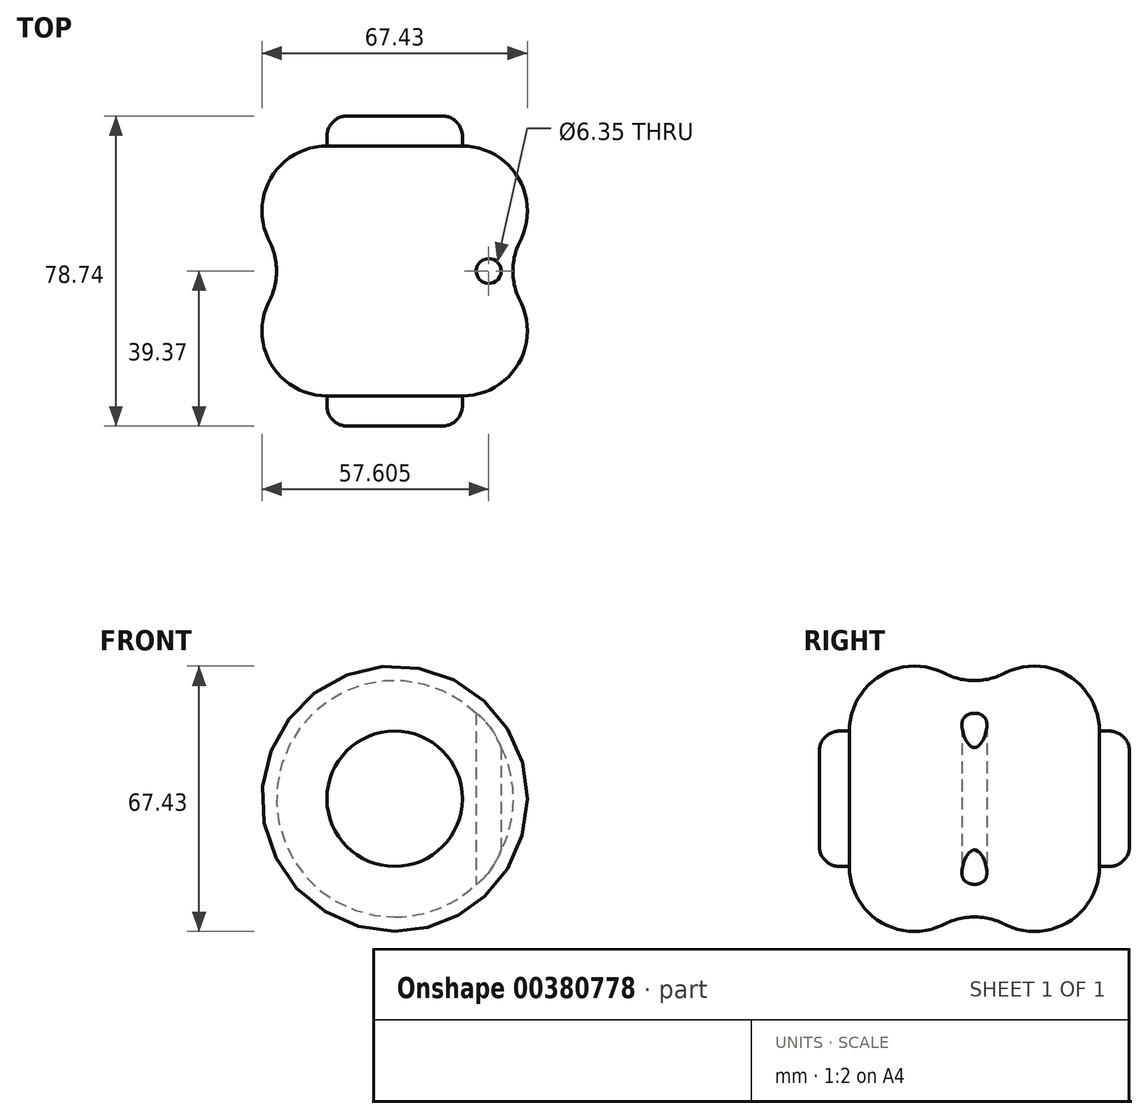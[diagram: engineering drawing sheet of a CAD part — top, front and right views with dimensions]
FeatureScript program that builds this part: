
annotation { "Feature Type Name" : "Feature", "Feature Type Description" : "" }
export const myFeature = defineFeature(function(context is Context, id is Id, definition is map)
    precondition{}
    {
        {
            var Q0;
            Q0=qCreatedBy(makeId("Front.planeOp"),FACE);
            var sketch = newSketch(context, id + "F0", { "sketchPlane" : qUnion([Q0])});
            skCircle(sketch, "E0", {"center": v(-32.36, 37.18) * mm, "radius": 28.31 * mm});
            skSolve(sketch);
        }
        {
            var Q0;
            Q0=makeQuery(id+"F0.imprint","IMPRINT",FACE,{"disambiguationData":[TD([[makeQuery(id+"F0.imprint","IMPRINT",EDGE,{"derivedFrom":sQuery(id+"F0.wireOp",EDGE,"E0")}),1.0]])]});
            extrude(context, id + "F1", {"entities" : qUnion([Q0]), "depth" : 31.75 * mm, "hasDraft" : true, "draftAngle" : 25 * degree, "hasSecondDirection" : true, "secondDirectionOppositeDirection" : true, "secondDirectionDepth" : 31.75 * mm, "hasSecondDirectionDraft" : true, "secondDirectionDraftAngle" : 25 * degree});
        }
        {
            var Q0;
            Q0=makeQuery(id+"F1.opExtrude","SWEPT_FACE",FACE,{"disambiguationData":[OSD([sQuery(id+"F0.wireOp",EDGE,"E0")])]});
            var Q1;
            Q1=makeQuery(id+"F1.opExtrude","CAP_FACE",FACE,{"disambiguationData":[OSD([sQuery(id+"F0.wireOp",EDGE,"E0")])],"isStart":false});
            fillet(context, id + "F2", {"entities" : qUnion([Q0, Q1]), "radius" : 16.5 * mm, "tangentPropagation" : true, "allowEdgeOverflow" : false});
        }
        {
            var Q0;
            Q0=qCreatedBy(makeId("Top.planeOp"),FACE);
            var sketch = newSketch(context, id + "F3", { "sketchPlane" : qUnion([Q0])});
            skPoint(sketch, "E1", {"position": v(-8.47, 0) * mm});
            skSolve(sketch);
        }
        {
            var Q0;
            Q0=sQuery(id+"F3.wireOp",VERTEX,"E1");
            var Q1;
            Q1=makeQuery(id+"F1.*.split.splitOp","SPLIT",BODY,{"derivedFrom":makeQuery(id+"F1.opExtrude","SWEPT_BODY",BODY,{"disambiguationData":[OSD([sQuery(id+"F0.wireOp",EDGE,"E0")])]})});
            hole(context, id + "F4", {"style" : HoleStyle.SIMPLE, "endStyle" : HoleEndStyle.THROUGH, "oppositeDirection" : true, "holeDiameter" : 6.35 * mm, "isTappedThrough" : true, "tappedDepth" : 12.7 * mm, "tapClearance" : 3, "locations" : qUnion([Q0]), "scope" : qUnion([Q1])});
        }
        {
            var Q0;
            Q0=makeQuery(id+"F1.opExtrude","CAP_FACE",FACE,{"disambiguationData":[OSD([sQuery(id+"F0.wireOp",EDGE,"E0")])],"isStart":false});
            var Q1;
            Q1=makeQuery(id+"F1.opExtrude","CAP_FACE",FACE,{"disambiguationData":[OSD([sQuery(id+"F0.wireOp",EDGE,"E0")])],"isStart":true});
            extrude(context, id + "F5", {"entities" : qUnion([Q0, Q1]), "operationType" : NewBodyOperationType.ADD, "depth" : 7.62 * mm, "hasSecondDirection" : true, "secondDirectionOppositeDirection" : true, "secondDirectionDepth" : 7.62 * mm});
        }
        {
            var Q0;
            {var subQ0=sQuery(id+"F0.wireOp",EDGE,"E0");Q0=makeQuery(id+"F5.opExtrude","CAP_FACE",FACE,{"disambiguationData":[OSD([subQ0]),TDD([makeQuery(id+"F1.opExtrude","CAP_FACE",FACE,{"disambiguationData":[OSD([subQ0])],"isStart":false})])],"isStart":false});}
            var Q1;
            {var subQ0=sQuery(id+"F0.wireOp",EDGE,"E0");Q1=makeQuery(id+"F5.opExtrude","CAP_FACE",FACE,{"disambiguationData":[OSD([subQ0]),TDD([makeQuery(id+"F1.opExtrude","CAP_FACE",FACE,{"disambiguationData":[OSD([subQ0])],"isStart":true})])],"isStart":true});}
            fillet(context, id + "F6", {"entities" : qUnion([Q0, Q1]), "radius" : 5.08 * mm, "tangentPropagation" : true, "allowEdgeOverflow" : false});
        }
    });
